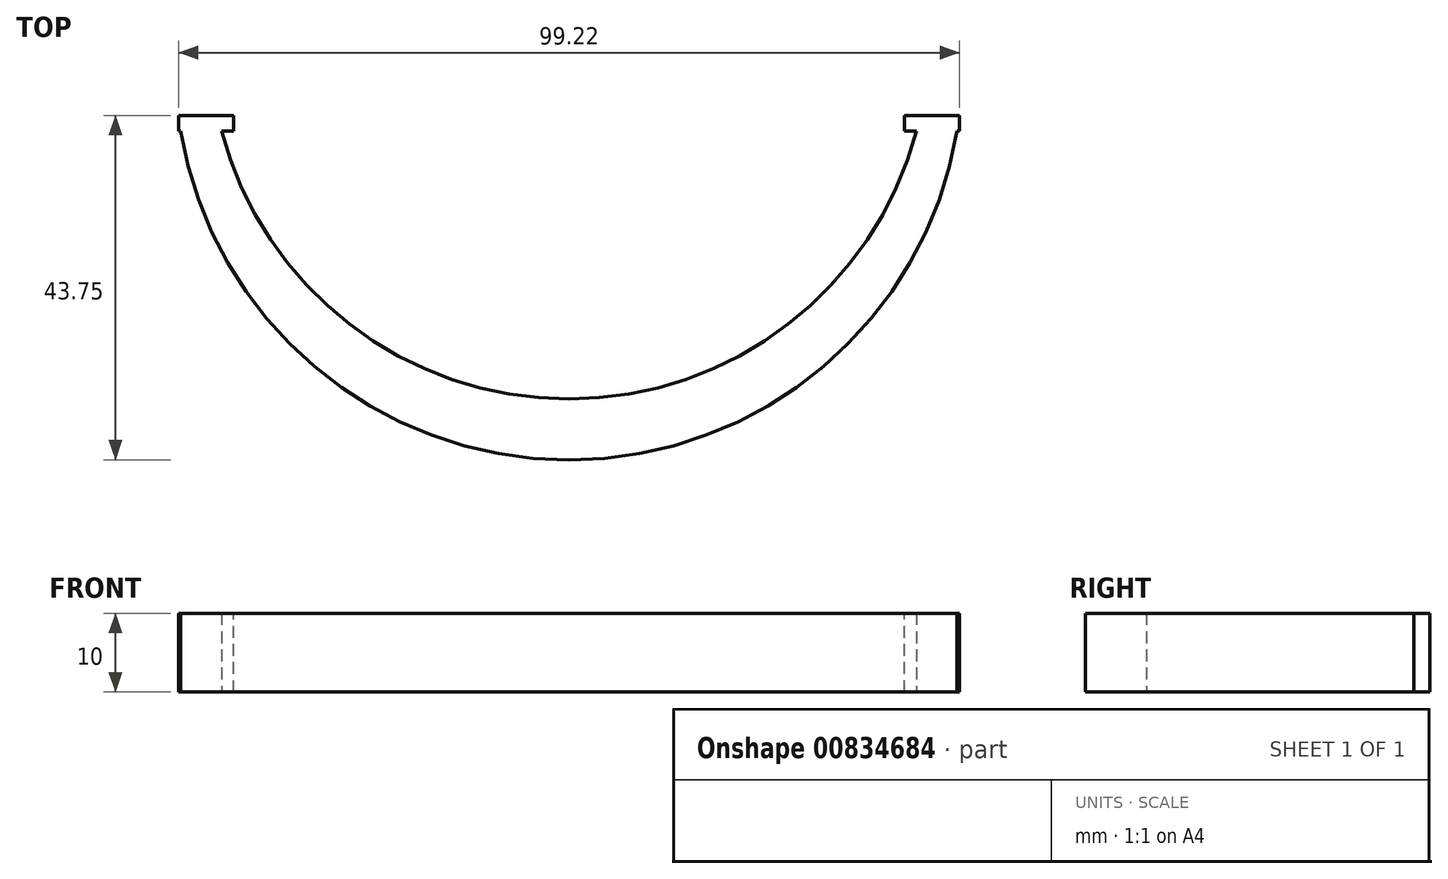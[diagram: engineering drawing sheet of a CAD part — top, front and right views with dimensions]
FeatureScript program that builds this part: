
annotation { "Feature Type Name" : "Feature", "Feature Type Description" : "" }
export const myFeature = defineFeature(function(context is Context, id is Id, definition is map)
    precondition{}
    {
        {
            var Q0;
            Q0=qCreatedBy(makeId("Top.planeOp"),FACE);
            var sketch = newSketch(context, id + "F0", { "sketchPlane" : qUnion([Q0])});
            skCircle(sketch, "E0", {"center": v(0, 0) * mm, "radius": 50 * mm});
            skCircle(sketch, "E1", {"center": v(0, 3.37) * mm, "radius": 45.63 * mm});
            skLineSegment(sketch, "E2", {"start": v(-49.6, -6.25) * mm, "end": v(49.6, -6.25) * mm});
            skPoint(sketch, "E3", {"position": v(-44.6, -6.25) * mm});
            skPoint(sketch, "E4", {"position": v(44.6, -6.25) * mm});
            skPoint(sketch, "E5", {"position": v(0, 50) * mm});
            skSolve(sketch);
        }
        {
            var Q0;
            {var subQ0=sQuery(id+"F0.wireOp",EDGE,"E2");var subQ1=sQuery(id+"F0.wireOp",EDGE,"E0");var subQ2=makeQuery(id+"F0.imprint","INTERSECT",VERTEX,{"disambiguationData":[OD(0.0)],"derivedFrom":[subQ1,subQ0]});Q0=makeQuery(id+"F0.imprint","IMPRINT",FACE,{"disambiguationData":[TD([[makeQuery(id+"F0.imprint","IMPRINT",EDGE,{"disambiguationData":[TD([[subQ2,1.0]])],"derivedFrom":subQ1}),1.0]])]});}
            var Q1;
            {var subQ0=sQuery(id+"F0.wireOp",EDGE,"E2");var subQ1=sQuery(id+"F0.wireOp",EDGE,"E0");var subQ2=makeQuery(id+"F0.imprint","INTERSECT",VERTEX,{"disambiguationData":[OD(1.0)],"derivedFrom":[subQ1,subQ0]});Q1=makeQuery(id+"F0.imprint","IMPRINT",FACE,{"disambiguationData":[TD([[makeQuery(id+"F0.imprint","IMPRINT",EDGE,{"disambiguationData":[TD([[subQ2,-1.0]])],"derivedFrom":subQ1}),1.0]])]});}
            extrude(context, id + "F1", {"entities" : qUnion([Q0, Q1]), "depth" : 10 * mm, "offsetDistance" : 25 * mm});
        }
        {
            var Q0;
            {var subQ0=sQuery(id+"F0.wireOp",EDGE,"E2");var subQ1=sQuery(id+"F0.wireOp",EDGE,"E0");var subQ2=makeQuery(id+"F0.imprint","INTERSECT",VERTEX,{"disambiguationData":[OD(0.0)],"derivedFrom":[subQ1,subQ0]});var subQ3=sQuery(id+"F0.wireOp",EDGE,"E1");var subQ5=makeQuery(id+"F0.imprint","INTERSECT",VERTEX,{"derivedFrom":[subQ1,subQ3]});Q0=makeQuery(id+"F1.opExtrude","CAP_FACE",FACE,{"disambiguationData":[OSD([subQ1,subQ3,subQ0]),TDD([makeQuery(id+"F0.imprint","IMPRINT",EDGE,{"disambiguationData":[TD([[subQ2,1.0]])],"derivedFrom":subQ1}),makeQuery(id+"F0.imprint","IMPRINT",EDGE,{"disambiguationData":[TD([[subQ5,-1.0]])],"derivedFrom":subQ3}),makeQuery(id+"F0.imprint","IMPRINT",EDGE,{"disambiguationData":[TD([[subQ2,-1.0]])],"derivedFrom":subQ0})])],"isStart":false});}
            var sketch = newSketch(context, id + "F2", { "sketchPlane" : qUnion([Q0])});
            skLineSegment(sketch, "E6.bottom", {"start": v(-49.6, -6.25) * mm, "end": v(-42.6, -6.25) * mm});
            skLineSegment(sketch, "E6.top", {"start": v(-49.6, -8.25) * mm, "end": v(-42.6, -8.25) * mm});
            skLineSegment(sketch, "E6.left", {"start": v(-49.6, -6.25) * mm, "end": v(-49.6, -8.25) * mm});
            skLineSegment(sketch, "E6.right", {"start": v(-42.6, -6.25) * mm, "end": v(-42.6, -8.25) * mm});
            skLineSegment(sketch, "E7.bottom", {"start": v(49.6, -6.25) * mm, "end": v(42.6, -6.25) * mm});
            skLineSegment(sketch, "E7.top", {"start": v(49.6, -8.25) * mm, "end": v(42.6, -8.25) * mm});
            skLineSegment(sketch, "E7.left", {"start": v(49.6, -6.25) * mm, "end": v(49.6, -8.25) * mm});
            skLineSegment(sketch, "E7.right", {"start": v(42.6, -6.25) * mm, "end": v(42.6, -8.25) * mm});
            skSolve(sketch);
        }
        {
            var Q0;
            Q0=qSketchRegion(id+"F2",true);
            extrude(context, id + "F3", {"entities" : qUnion([Q0]), "operationType" : NewBodyOperationType.ADD, "oppositeDirection" : true, "depth" : 10 * mm, "offsetDistance" : 25 * mm});
        }
    });
